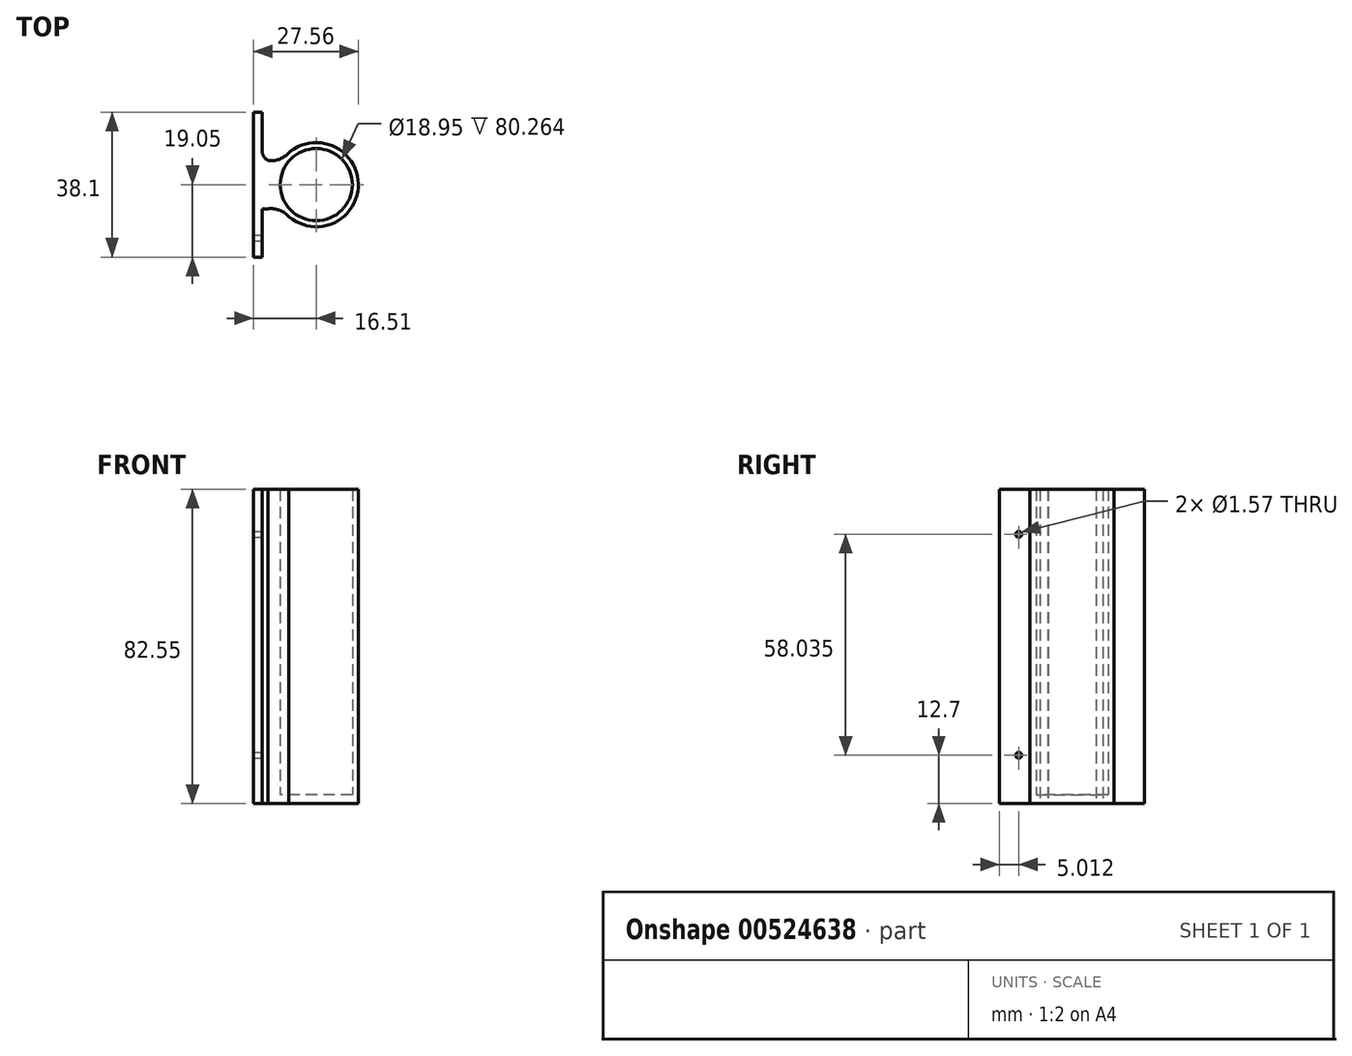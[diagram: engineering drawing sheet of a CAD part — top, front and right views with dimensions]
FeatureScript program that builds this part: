
annotation { "Feature Type Name" : "Feature", "Feature Type Description" : "" }
export const myFeature = defineFeature(function(context is Context, id is Id, definition is map)
    precondition{}
    {
        {
            var Q0;
            Q0=qCreatedBy(makeId("Top.planeOp"),FACE);
            var sketch = newSketch(context, id + "F0", { "sketchPlane" : qUnion([Q0])});
            skArc(sketch, "E0", {"start": v(-7.98, -7.64) * mm, "mid": v(11.05, -0.16) * mm, "end": v(-7.76, 7.87) * mm});
            skCircle(sketch, "E1", {"center": v(0, 0) * mm, "radius": 9.47 * mm});
            skLineSegment(sketch, "E2.0", {"start": v(-14.22, -6.35) * mm, "end": v(-14.22, 6.35) * mm});
            skLineSegment(sketch, "E3.0", {"start": v(-11.05, 6.35) * mm, "end": v(-14.22, 6.35) * mm});
            skLineSegment(sketch, "E4.0", {"start": v(-11.05, -6.35) * mm, "end": v(-14.22, -6.35) * mm});
            skArc(sketch, "E5", {"start": v(-12.64, 6.35) * mm, "mid": v(-9.87, 6.63) * mm, "end": v(-7.5, 8.1) * mm});
            skPoint(sketch, "E5.second.point", {"position": v(-7.5, 8.1) * mm});
            skPoint(sketch, "E5.third.point", {"position": v(-12.64, 6.35) * mm});
            skArc(sketch, "E6", {"start": v(-7.17, -8.4) * mm, "mid": v(-9.65, -6.7) * mm, "end": v(-12.64, -6.35) * mm});
            skPoint(sketch, "E6.second.point", {"position": v(-7.17, -8.4) * mm});
            skPoint(sketch, "E6.third.point", {"position": v(-12.64, -6.35) * mm});
            skSolve(sketch);
        }
        {
            var Q0;
            Q0=makeQuery(id+"F0.imprint","IMPRINT",FACE,{"disambiguationData":[TD([[makeQuery(id+"F0.imprint","IMPRINT",EDGE,{"derivedFrom":sQuery(id+"F0.wireOp",EDGE,"E1")}),-1.0]])]});
            extrude(context, id + "F1", {"entities" : qUnion([Q0]), "depth" : 82.55 * mm});
        }
        {
            var Q0;
            Q0=makeQuery(id+"F1.opExtrude","CAP_FACE",FACE,{"disambiguationData":[OSD([sQuery(id+"F0.wireOp",EDGE,"E0"),sQuery(id+"F0.wireOp",EDGE,"E1"),sQuery(id+"F0.wireOp",EDGE,"E2.0"),sQuery(id+"F0.wireOp",EDGE,"E3.0"),sQuery(id+"F0.wireOp",EDGE,"E4.0"),sQuery(id+"F0.wireOp",EDGE,"E5"),sQuery(id+"F0.wireOp",EDGE,"E6")])],"isStart":true});
            var sketch = newSketch(context, id + "F2", { "sketchPlane" : qUnion([Q0])});
            skCircle(sketch, "E7", {"center": v(0, 0) * mm, "radius": 9.47 * mm});
            skSolve(sketch);
        }
        {
            var Q0;
            Q0=qSketchRegion(id+"F2",true);
            extrude(context, id + "F3", {"entities" : qUnion([Q0]), "operationType" : NewBodyOperationType.ADD, "oppositeDirection" : true, "depth" : 2.3 * mm});
        }
        {
            var Q0;
            Q0=makeQuery(id+"F1.opExtrude","SWEPT_FACE",FACE,{"disambiguationData":[OSD([sQuery(id+"F0.wireOp",EDGE,"E2.0")])]});
            var sketch = newSketch(context, id + "F4", { "sketchPlane" : qUnion([Q0])});
            skLineSegment(sketch, "E8", {"start": v(0, 82.55) * mm, "end": v(19.05, 82.55) * mm});
            skLineSegment(sketch, "E9", {"start": v(0, 82.55) * mm, "end": v(-19.05, 82.55) * mm});
            skLineSegment(sketch, "E10", {"start": v(-19.05, 82.55) * mm, "end": v(-19.05, 0) * mm});
            skLineSegment(sketch, "E11", {"start": v(-19.05, 0) * mm, "end": v(19.05, 0) * mm});
            skLineSegment(sketch, "E12", {"start": v(19.05, 0) * mm, "end": v(19.05, 82.55) * mm});
            skSolve(sketch);
        }
        {
            var Q0;
            {var subQ2=sQuery(id+"F4.wireOp",EDGE,"E10");Q0=makeQuery(id+"F4.imprint","IMPRINT",FACE,{"disambiguationData":[TD([[makeQuery(id+"F4.imprint","IMPRINT",EDGE,{"derivedFrom":subQ2}),1.0]])]});}
            var Q1;
            {var subQ2=sQuery(id+"F4.wireOp",EDGE,"E12");Q1=makeQuery(id+"F4.imprint","IMPRINT",FACE,{"disambiguationData":[TD([[makeQuery(id+"F4.imprint","IMPRINT",EDGE,{"derivedFrom":subQ2}),1.0]])]});}
            var Q2;
            {var subQ1=sQuery(id+"F0.wireOp",EDGE,"E2.0");var subQ2=makeQuery(id+"F1.opExtrude","SWEPT_EDGE",EDGE,{"disambiguationData":[OSD([subQ1,sQuery(id+"F0.wireOp",EDGE,"E4.0")])]});Q2=makeQuery(id+"F4.imprint","IMPRINT",FACE,{"disambiguationData":[TD([[makeQuery(id+"F4.imprint","IMPRINT",EDGE,{"derivedFrom":subQ2}),-1.0]])]});}
            extrude(context, id + "F5", {"entities" : qUnion([Q0, Q1, Q2]), "operationType" : NewBodyOperationType.ADD, "depth" : 2.3 * mm, "offsetDistance" : 25.4 * mm});
        }
        {
            var Q0;
            Q0=makeQuery(id+"F1.opExtrude","SWEPT_EDGE",EDGE,{"disambiguationData":[OSD([sQuery(id+"F0.wireOp",EDGE,"E2.0"),sQuery(id+"F0.wireOp",EDGE,"E4.0")])]});
            var Q1;
            Q1=makeQuery(id+"F1.opExtrude","SWEPT_EDGE",EDGE,{"disambiguationData":[OSD([sQuery(id+"F0.wireOp",EDGE,"E2.0"),sQuery(id+"F0.wireOp",EDGE,"E3.0")])]});
            fillet(context, id + "F6", {"entities" : qUnion([Q0, Q1]), "radius" : 3.05 * mm, "tangentPropagation" : true, "allowEdgeOverflow" : false});
        }
        {
            var Q0;
            {var subQ2=sQuery(id+"F0.wireOp",EDGE,"E4.0");var subQ7=sQuery(id+"F4.wireOp",EDGE,"E9");var subQ8=sQuery(id+"F4.wireOp",EDGE,"E8");var subQ9=sQuery(id+"F4.wireOp",EDGE,"E11");var subQ10=sQuery(id+"F4.wireOp",EDGE,"E12");Q0=makeQuery(id+"F5.boolean.opBoolean","SPLIT",FACE,{"disambiguationData":[TD([makeQuery(id+"F1.opExtrude","SWEPT_FACE",FACE,{"disambiguationData":[OSD([subQ2])]})])],"derivedFrom":makeQuery(id+"F5.opExtrude","CAP_FACE",FACE,{"disambiguationData":[OSD([subQ8,subQ7,sQuery(id+"F4.wireOp",EDGE,"E10"),subQ9,subQ10])],"isStart":true})});}
            var sketch = newSketch(context, id + "F7", { "sketchPlane" : qUnion([Q0])});
            skPoint(sketch, "E13", {"position": v(-14.04, 70.74) * mm});
            skCircle(sketch, "E14", {"center": v(-14.04, 70.74) * mm, "radius": 0.79 * mm});
            skPoint(sketch, "E15", {"position": v(-14.04, 12.7) * mm});
            skCircle(sketch, "E16", {"center": v(-14.04, 12.7) * mm, "radius": 0.79 * mm});
            skSolve(sketch);
        }
        {
            var Q0;
            Q0 = qSketchRegion(id + "F7", true);
            extrude(context, id + "F8", {"entities" : qUnion([Q0]), "operationType" : NewBodyOperationType.REMOVE, "oppositeDirection" : true, "depth" : 13.2 * mm, "offsetDistance" : 25.4 * mm});
        }
    });
